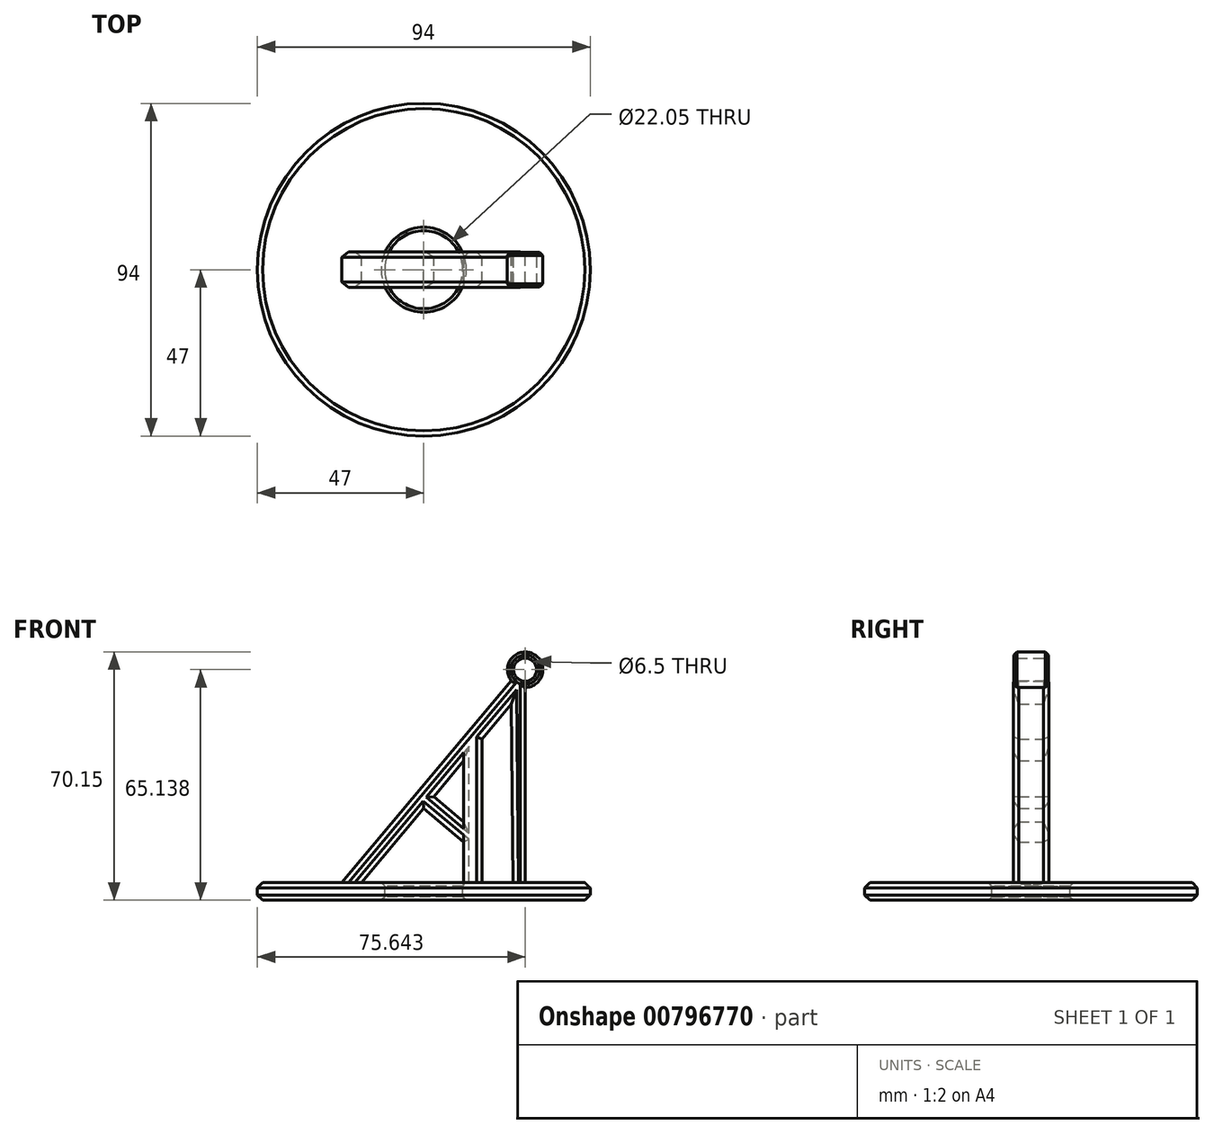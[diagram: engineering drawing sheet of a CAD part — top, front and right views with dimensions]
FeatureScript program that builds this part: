
annotation { "Feature Type Name" : "Feature", "Feature Type Description" : "" }
export const myFeature = defineFeature(function(context is Context, id is Id, definition is map)
    precondition{}
    {
        {
            var Q0;
            Q0=qCreatedBy(makeId("Top.planeOp"),FACE);
            var sketch = newSketch(context, id + "F0", { "sketchPlane" : qUnion([Q0])});
            skCircle(sketch, "E0", {"center": v(0, 0) * mm, "radius": 47 * mm});
            skCircle(sketch, "E1", {"center": v(0, 0) * mm, "radius": 11.03 * mm});
            skSolve(sketch);
        }
        {
            var Q0;
            Q0=makeQuery(id+"F0.imprint","IMPRINT",FACE,{"disambiguationData":[TD([[makeQuery(id+"F0.imprint","IMPRINT",EDGE,{"derivedFrom":sQuery(id+"F0.wireOp",EDGE,"E0")}),1.0]])]});
            extrude(context, id + "F1", {"entities" : qUnion([Q0]), "oppositeDirection" : true, "depth" : 5 * mm, "offsetDistance" : 25.4 * mm});
        }
        {
            var Q0;
            Q0=qCreatedBy(makeId("Front.planeOp"),FACE);
            var sketch = newSketch(context, id + "F2", { "sketchPlane" : qUnion([Q0])});
            skLineSegment(sketch, "E2", {"start": v(-23.17, 0) * mm, "end": v(0, 27.62) * mm});
            skLineSegment(sketch, "E3", {"start": v(-23.17, 0) * mm, "end": v(-17.55, 0) * mm});
            skLineSegment(sketch, "E4", {"start": v(-17.55, 0) * mm, "end": v(0, 20.92) * mm});
            skLineSegment(sketch, "E5", {"start": v(-17.55, 0) * mm, "end": v(-9.13, 0) * mm});
            skLineSegment(sketch, "E6", {"start": v(0, 20.92) * mm, "end": v(12.54, 35.86) * mm});
            skLineSegment(sketch, "E7", {"start": v(0, 27.62) * mm, "end": v(9.68, 39.15) * mm});
            skLineSegment(sketch, "E8", {"start": v(46.82, 0) * mm, "end": v(46.82, 56.77) * mm});
            skLineSegment(sketch, "E9", {"start": v(12.54, 35.86) * mm, "end": v(28.7, 55.12) * mm});
            skLineSegment(sketch, "E10", {"start": v(9.68, 39.15) * mm, "end": v(24.7, 57.05) * mm});
            skCircle(sketch, "E11", {"center": v(28.64, 60.14) * mm, "radius": 5.01 * mm});
            skPoint(sketch, "E11.third.point", {"position": v(31.55, 64.22) * mm});
            skCircle(sketch, "E12", {"center": v(28.64, 60.14) * mm, "radius": 3.25 * mm});
            skLineSegment(sketch, "E13", {"start": v(11.28, 0) * mm, "end": v(11.28, 34.36) * mm});
            skLineSegment(sketch, "E14", {"start": v(11.28, 34.36) * mm, "end": v(16.47, 40.54) * mm});
            skLineSegment(sketch, "E15", {"start": v(16.47, 40.54) * mm, "end": v(16.47, 0) * mm});
            skLineSegment(sketch, "E16", {"start": v(16.47, 0) * mm, "end": v(11.28, 0) * mm});
            skLineSegment(sketch, "E17", {"start": v(28.7, 55.12) * mm, "end": v(28.7, 0) * mm});
            skLineSegment(sketch, "E18", {"start": v(28.7, 0) * mm, "end": v(25.28, 0) * mm});
            skLineSegment(sketch, "E19", {"start": v(25.28, 0) * mm, "end": v(24.73, 50.39) * mm});
            skLineSegment(sketch, "E20", {"start": v(24.73, 50.39) * mm, "end": v(28.7, 55.12) * mm});
            skLineSegment(sketch, "E21", {"start": v(11.28, 17.18) * mm, "end": v(2.82, 24.28) * mm});
            skLineSegment(sketch, "E22", {"start": v(2.82, 24.28) * mm, "end": v(0, 20.92) * mm});
            skLineSegment(sketch, "E23", {"start": v(0, 20.92) * mm, "end": v(11.28, 11.46) * mm});
            skSolve(sketch);
        }
        {
            var Q0;
            Q0=makeQuery(id+"F2.imprint","IMPRINT",FACE,{"disambiguationData":[TD([[makeQuery(id+"F2.imprint","IMPRINT",EDGE,{"derivedFrom":sQuery(id+"F2.wireOp",EDGE,"E17")}),-1.0]])]});
            var Q1;
            Q1=makeQuery(id+"F2.imprint","IMPRINT",FACE,{"disambiguationData":[TD([[makeQuery(id+"F2.imprint","IMPRINT",EDGE,{"derivedFrom":sQuery(id+"F2.wireOp",EDGE,"E13")}),-1.0]])]});
            var Q2;
            Q2=makeQuery(id+"F2.imprint","IMPRINT",FACE,{"disambiguationData":[TD([[makeQuery(id+"F2.imprint","IMPRINT",EDGE,{"derivedFrom":sQuery(id+"F2.wireOp",EDGE,"E2")}),-1.0]])]});
            var Q3;
            Q3=makeQuery(id+"F2.imprint","IMPRINT",FACE,{"disambiguationData":[TD([[makeQuery(id+"F2.imprint","IMPRINT",EDGE,{"derivedFrom":sQuery(id+"F2.wireOp",EDGE,"E12")}),-1.0]])]});
            var Q4;
            {var subQ0=sQuery(id+"F2.wireOp",EDGE,"E21");Q4=makeQuery(id+"F2.imprint","IMPRINT",FACE,{"disambiguationData":[TD([[makeQuery(id+"F2.imprint","IMPRINT",EDGE,{"derivedFrom":subQ0}),1.0]])]});}
            extrude(context, id + "F3", {"entities" : qUnion([Q0, Q1, Q2, Q3, Q4]), "operationType" : NewBodyOperationType.ADD, "endBound" : BoundingType.SYMMETRIC, "depth" : 10 * mm, "offsetDistance" : 25.4 * mm});
        }
        {
            var Q0;
            Q0=makeQuery(id+"F3.opExtrude","CAP_EDGE",EDGE,{"disambiguationData":[OSD([sQuery(id+"F2.wireOp",EDGE,"E12")])],"isStart":false});
            var Q1;
            Q1=makeQuery(id+"F3.opExtrude","CAP_EDGE",EDGE,{"disambiguationData":[OSD([sQuery(id+"F2.wireOp",EDGE,"E12")])],"isStart":true});
            chamfer(context, id + "F4", {"entities" : qUnion([Q0, Q1]), "width" : 1 * mm, "tangentPropagation" : true});
        }
        {
            var Q0;
            Q0=makeQuery(id+"F3.opExtrude","CAP_EDGE",EDGE,{"disambiguationData":[OSD([sQuery(id+"F2.wireOp",EDGE,"E15")])],"isStart":false});
            var Q1;
            Q1=makeQuery(id+"F3.opExtrude","CAP_EDGE",EDGE,{"disambiguationData":[OSD([sQuery(id+"F2.wireOp",EDGE,"E6"),sQuery(id+"F2.wireOp",EDGE,"E9")])],"isStart":false});
            var Q2;
            Q2=makeQuery(id+"F3.opExtrude","CAP_EDGE",EDGE,{"disambiguationData":[OSD([sQuery(id+"F2.wireOp",EDGE,"E19")])],"isStart":false});
            var Q3;
            Q3=makeQuery(id+"F3.opExtrude","CAP_EDGE",EDGE,{"disambiguationData":[OSD([sQuery(id+"F2.wireOp",EDGE,"E15")])],"isStart":true});
            var Q4;
            Q4=makeQuery(id+"F3.opExtrude","CAP_EDGE",EDGE,{"disambiguationData":[OSD([sQuery(id+"F2.wireOp",EDGE,"E6"),sQuery(id+"F2.wireOp",EDGE,"E9")])],"isStart":true});
            var Q5;
            Q5=makeQuery(id+"F3.opExtrude","CAP_EDGE",EDGE,{"disambiguationData":[OSD([sQuery(id+"F2.wireOp",EDGE,"E19")])],"isStart":true});
            var Q6;
            Q6=makeQuery(id+"F3.opExtrude","CAP_EDGE",EDGE,{"disambiguationData":[OSD([sQuery(id+"F2.wireOp",EDGE,"E17")])],"isStart":true});
            var Q7;
            Q7=makeQuery(id+"F3.opExtrude","CAP_EDGE",EDGE,{"disambiguationData":[OSD([sQuery(id+"F2.wireOp",EDGE,"E17")])],"isStart":false});
            var Q8;
            Q8=makeQuery(id+"F3.opExtrude","CAP_EDGE",EDGE,{"disambiguationData":[OSD([sQuery(id+"F2.wireOp",EDGE,"E4"),sQuery(id+"F2.wireOp",EDGE,"E6")])],"isStart":true});
            var Q9;
            Q9=makeQuery(id+"F3.opExtrude","CAP_EDGE",EDGE,{"disambiguationData":[OSD([sQuery(id+"F2.wireOp",EDGE,"E4"),sQuery(id+"F2.wireOp",EDGE,"E6")])],"isStart":false});
            var Q10;
            Q10=makeQuery(id+"F3.opExtrude","CAP_EDGE",EDGE,{"disambiguationData":[OSD([sQuery(id+"F2.wireOp",EDGE,"E13")])],"isStart":true});
            var Q11;
            Q11=makeQuery(id+"F3.opExtrude","CAP_EDGE",EDGE,{"disambiguationData":[OSD([sQuery(id+"F2.wireOp",EDGE,"E2"),sQuery(id+"F2.wireOp",EDGE,"E7"),sQuery(id+"F2.wireOp",EDGE,"E10")])],"isStart":true});
            var Q12;
            Q12=makeQuery(id+"F3.opExtrude","CAP_EDGE",EDGE,{"disambiguationData":[OSD([sQuery(id+"F2.wireOp",EDGE,"E2"),sQuery(id+"F2.wireOp",EDGE,"E7"),sQuery(id+"F2.wireOp",EDGE,"E10")])],"isStart":false});
            var Q13;
            Q13=makeQuery(id+"F3.opExtrude","CAP_EDGE",EDGE,{"disambiguationData":[OSD([sQuery(id+"F2.wireOp",EDGE,"E21")])],"isStart":false});
            var Q14;
            Q14=makeQuery(id+"F3.opExtrude","CAP_EDGE",EDGE,{"disambiguationData":[OSD([sQuery(id+"F2.wireOp",EDGE,"E23")])],"isStart":false});
            var Q15;
            Q15=makeQuery(id+"F3.opExtrude","CAP_EDGE",EDGE,{"disambiguationData":[OSD([sQuery(id+"F2.wireOp",EDGE,"E21")])],"isStart":true});
            var Q16;
            Q16=makeQuery(id+"F3.opExtrude","CAP_EDGE",EDGE,{"disambiguationData":[OSD([sQuery(id+"F2.wireOp",EDGE,"E23")])],"isStart":true});
            chamfer(context, id + "F5", {"entities" : qUnion([Q0, Q1, Q2, Q3, Q4, Q5, Q6, Q7, Q8, Q9, Q10, Q11, Q12, Q13, Q14, Q15, Q16]), "width" : 1.5 * mm, "tangentPropagation" : true});
        }
        {
            var Q0;
            Q0=makeQuery(id+"F3.opExtrude","CAP_EDGE",EDGE,{"disambiguationData":[OSD([sQuery(id+"F2.wireOp",EDGE,"E11")])],"isStart":false});
            var Q1;
            Q1=makeQuery(id+"F3.opExtrude","CAP_EDGE",EDGE,{"disambiguationData":[OSD([sQuery(id+"F2.wireOp",EDGE,"E11")])],"isStart":true});
            chamfer(context, id + "F6", {"entities" : qUnion([Q0, Q1]), "width" : 1 * mm, "tangentPropagation" : true});
        }
        {
            var Q0;
            Q0=makeQuery(id+"F1.opExtrude","CAP_EDGE",EDGE,{"disambiguationData":[OSD([sQuery(id+"F0.wireOp",EDGE,"E0")])],"isStart":true});
            var Q1;
            Q1=makeQuery(id+"F1.opExtrude","CAP_EDGE",EDGE,{"disambiguationData":[OSD([sQuery(id+"F0.wireOp",EDGE,"E0")])],"isStart":false});
            chamfer(context, id + "F7", {"entities" : qUnion([Q0, Q1]), "width" : 1.5 * mm, "tangentPropagation" : true});
        }
        {
            var Q0;
            Q0=makeQuery(id+"F1.opExtrude","CAP_EDGE",EDGE,{"disambiguationData":[OSD([sQuery(id+"F0.wireOp",EDGE,"E1")])],"isStart":true});
            var Q1;
            Q1=makeQuery(id+"F1.opExtrude","CAP_EDGE",EDGE,{"disambiguationData":[OSD([sQuery(id+"F0.wireOp",EDGE,"E1")])],"isStart":false});
            chamfer(context, id + "F8", {"entities" : qUnion([Q0, Q1]), "width" : 1 * mm, "tangentPropagation" : true});
        }
    });
